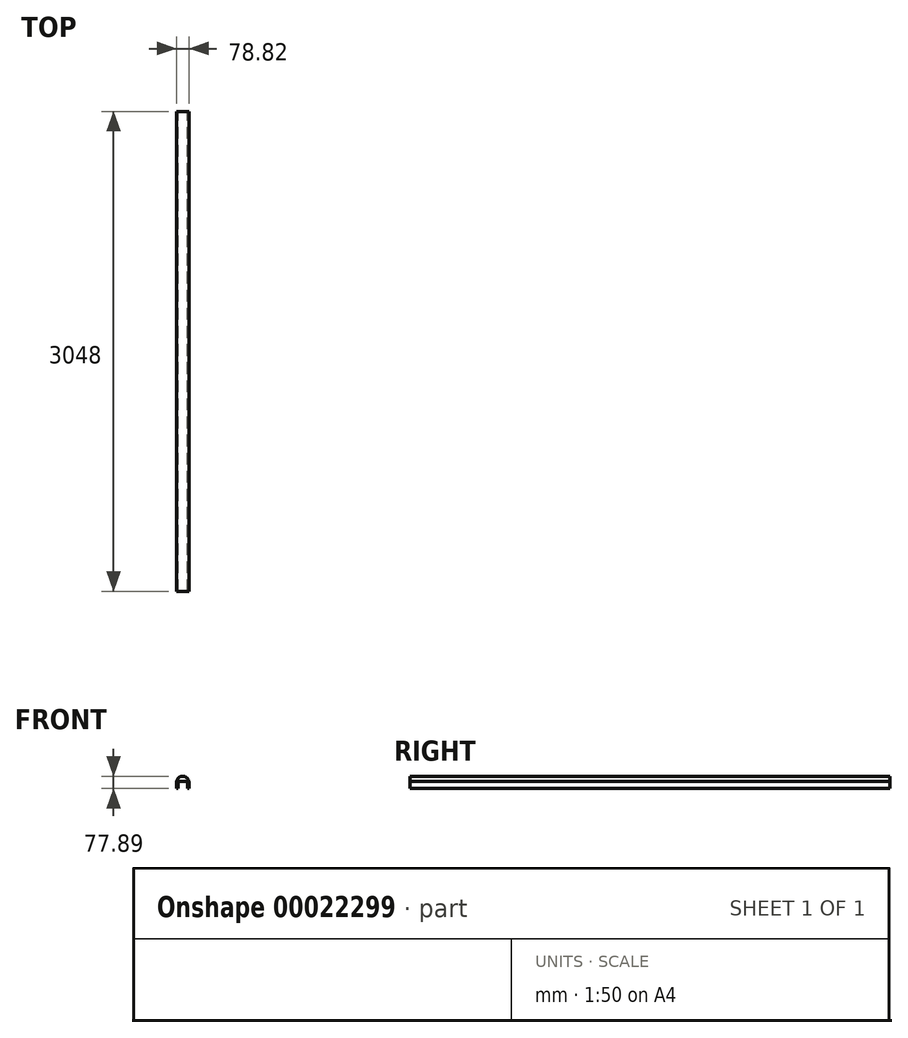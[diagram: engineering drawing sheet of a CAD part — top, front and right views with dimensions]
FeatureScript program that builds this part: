
annotation { "Feature Type Name" : "Feature", "Feature Type Description" : "" }
export const myFeature = defineFeature(function(context is Context, id is Id, definition is map)
    precondition{}
    {
        {
            var Q0;
            Q0=qCreatedBy(makeId("Front.planeOp"),FACE);
            var sketch = newSketch(context, id + "F0", { "sketchPlane" : qUnion([Q0])});
            skLineSegment(sketch, "E0", {"start": v(0, 0) * mm, "end": v(0, 46.47) * mm});
            skArc(sketch, "E1", {"start": v(78.82, 46.47) * mm, "mid": v(39.4, 77.89) * mm, "end": v(0, 46.47) * mm});
            skLineSegment(sketch, "E2", {"start": v(78.82, 46.47) * mm, "end": v(78.82, 0) * mm});
            skLineSegment(sketch, "E3", {"start": v(0, 0) * mm, "end": v(8.98, 0) * mm});
            skLineSegment(sketch, "E4", {"start": v(8.98, 0) * mm, "end": v(8.98, 46.28) * mm});
            skLineSegment(sketch, "E5", {"start": v(8.98, 46.28) * mm, "end": v(70.57, 46.28) * mm});
            skLineSegment(sketch, "E6", {"start": v(70.57, 46.28) * mm, "end": v(70.57, 0) * mm});
            skLineSegment(sketch, "E7", {"start": v(70.57, 0) * mm, "end": v(78.82, 0) * mm});
            skSolve(sketch);
        }
        {
            var Q0;
            Q0 = qSketchRegion(id + "F0", true);
            extrude(context, id + "F1", {"entities" : qUnion([Q0]), "depth" : 3048 * mm});
        }
    });
